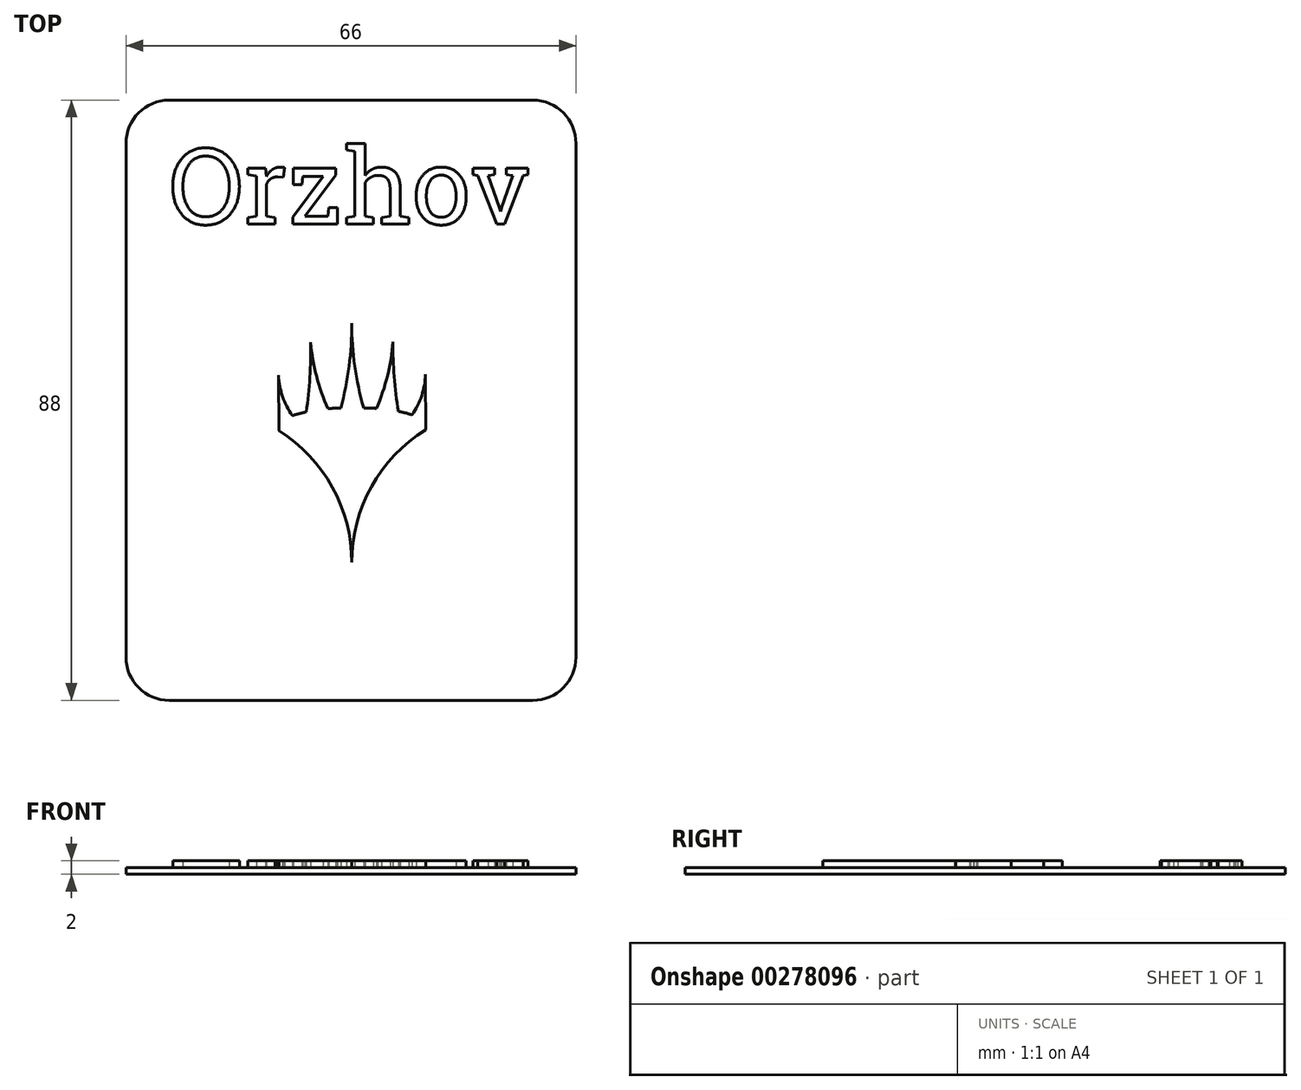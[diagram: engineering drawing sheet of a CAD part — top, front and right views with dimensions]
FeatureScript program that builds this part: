
annotation { "Feature Type Name" : "Feature", "Feature Type Description" : "" }
export const myFeature = defineFeature(function(context is Context, id is Id, definition is map)
    precondition{}
    {
        {
            var Q0;
            Q0=qCreatedBy(makeId("Top.planeOp"),FACE);
            var sketch = newSketch(context, id + "F0", { "sketchPlane" : qUnion([Q0])});
            skLineSegment(sketch, "E0.bottom", {"start": v(-27.42, 35.05) * mm, "end": v(29.8, 35.05) * mm});
            skLineSegment(sketch, "E0.top", {"start": v(-27.42, -41.25) * mm, "end": v(29.8, -41.25) * mm});
            skLineSegment(sketch, "E0.left", {"start": v(-27.42, 35.05) * mm, "end": v(-27.42, -41.25) * mm});
            skLineSegment(sketch, "E0.right", {"start": v(29.8, 35.05) * mm, "end": v(29.8, -41.25) * mm});
            skArc(sketch, "E1", {"start": v(0.12, -23.8) * mm, "mid": v(-2.72, -12.76) * mm, "end": v(-10.54, -4.47) * mm});
            skArc(sketch, "E2", {"start": v(10.94, -4.34) * mm, "mid": v(3, -12.67) * mm, "end": v(0.12, -23.8) * mm});
            skLineSegment(sketch, "E3", {"start": v(-10.54, -4.47) * mm, "end": v(-10.62, 4.28) * mm});
            skArc(sketch, "E4", {"start": v(-5.93, 8.51) * mm, "mid": v(-5.06, 3.53) * mm, "end": v(-3.38, -1.24) * mm});
            skArc(sketch, "E5", {"start": v(-10.62, 4.28) * mm, "mid": v(-10.13, 0.85) * mm, "end": v(-8.59, -2.24) * mm});
            skArc(sketch, "E6", {"start": v(-6.58, -1.72) * mm, "mid": v(-7.6, -1.95) * mm, "end": v(-8.59, -2.24) * mm});
            skArc(sketch, "E7", {"start": v(-1.5, -1.15) * mm, "mid": v(-2.44, -1.17) * mm, "end": v(-3.38, -1.24) * mm});
            skArc(sketch, "E8", {"start": v(-1.5, -1.15) * mm, "mid": v(-0.28, 5.01) * mm, "end": v(0.1, 11.29) * mm});
            skArc(sketch, "E9.MirrorCS", {"start": v(1.86, -1.13) * mm, "mid": v(0.56, 5.02) * mm, "end": v(0.1, 11.29) * mm});
            skArc(sketch, "E10", {"start": v(-6.58, -1.72) * mm, "mid": v(-6.02, 3.38) * mm, "end": v(-5.93, 8.51) * mm});
            skLineSegment(sketch, "E11.MirrorCS", {"start": v(10.94, -4.34) * mm, "end": v(10.9, 4.4) * mm});
            skArc(sketch, "E12.MirrorCS", {"start": v(10.9, 4.4) * mm, "mid": v(10.46, 0.98) * mm, "end": v(8.96, -2.14) * mm});
            skArc(sketch, "E13.MirrorCS", {"start": v(6.94, -1.64) * mm, "mid": v(7.96, -1.85) * mm, "end": v(8.96, -2.14) * mm});
            skArc(sketch, "E14.MirrorCS", {"start": v(6.94, -1.64) * mm, "mid": v(6.33, 3.46) * mm, "end": v(6.16, 8.59) * mm});
            skArc(sketch, "E15.MirrorCS", {"start": v(6.16, 8.59) * mm, "mid": v(5.36, 3.6) * mm, "end": v(3.73, -1.2) * mm});
            skArc(sketch, "E16.MirrorCS", {"start": v(1.86, -1.13) * mm, "mid": v(2.8, -1.13) * mm, "end": v(3.73, -1.2) * mm});
            skSolve(sketch);
        }
        {
            var Q0;
            {var subQ4=sQuery(id+"F0.wireOp",EDGE,"E1");Q0=makeQuery(id+"F0.imprint","IMPRINT",FACE,{"disambiguationData":[TD([[makeQuery(id+"F0.imprint","IMPRINT",EDGE,{"derivedFrom":subQ4}),-1.0]])]});}
            extrude(context, id + "F1", {"entities" : qUnion([Q0]), "depth" : 2 * mm});
        }
        {
            var Q0;
            Q0=qCreatedBy(makeId("Top.planeOp"),FACE);
            var sketch = newSketch(context, id + "F2", { "sketchPlane" : qUnion([Q0])});
            skLineSegment(sketch, "E17.bottom", {"start": v(-26.65, 44) * mm, "end": v(26.65, 44) * mm});
            skLineSegment(sketch, "E17.top", {"start": v(-26.65, -44) * mm, "end": v(26.65, -44) * mm});
            skLineSegment(sketch, "E17.left", {"start": v(-33, 37.65) * mm, "end": v(-33, -37.65) * mm});
            skLineSegment(sketch, "E17.right", {"start": v(33, 37.65) * mm, "end": v(33, -37.65) * mm});
            skPoint(sketch, "E18.visualSharp", {"position": v(-33, 44) * mm});
            skArc(sketch, "E18.filletArc", {"start": v(-26.65, 44) * mm, "mid": v(-31.14, 42.14) * mm, "end": v(-33, 37.65) * mm});
            skPoint(sketch, "E19.visualSharp", {"position": v(33, 44) * mm});
            skArc(sketch, "E19.filletArc", {"start": v(33, 37.65) * mm, "mid": v(31.14, 42.14) * mm, "end": v(26.65, 44) * mm});
            skPoint(sketch, "E20.visualSharp", {"position": v(-33, -44) * mm});
            skArc(sketch, "E20.filletArc", {"start": v(-33, -37.65) * mm, "mid": v(-31.14, -42.14) * mm, "end": v(-26.65, -44) * mm});
            skPoint(sketch, "E21.visualSharp", {"position": v(33, -44) * mm});
            skArc(sketch, "E21.filletArc", {"start": v(26.65, -44) * mm, "mid": v(31.14, -42.14) * mm, "end": v(33, -37.65) * mm});
            skSolve(sketch);
        }
        {
            var Q0;
            Q0=makeQuery(id+"F2.imprint","IMPRINT",FACE,{"disambiguationData":[TD([[makeQuery(id+"F2.imprint","IMPRINT",EDGE,{"derivedFrom":sQuery(id+"F2.wireOp",EDGE,"E17.bottom")}),-1.0]])]});
            extrude(context, id + "F3", {"entities" : qUnion([Q0]), "operationType" : NewBodyOperationType.ADD, "depth" : 1 * mm});
        }
        {
            var Q0;
            Q0=qCreatedBy(makeId("Top.planeOp"),FACE);
            var sketch = newSketch(context, id + "F4", { "sketchPlane" : qUnion([Q0])});
            skText(sketch, "E22", { "text": "Orzhov", "fontName": "RobotoSlab-Regular.ttf"});
            const initialGuessF4  = {"E22": [-0.02674, 0.02583, 1, 0, 0.01118]};
            skSetInitialGuess(sketch, initialGuessF4);
            skSolve(sketch);
        }
        {
            var Q0;
            Q0 = qSketchRegion(id + "F4", true);
            extrude(context, id + "F5", {"entities" : qUnion([Q0]), "operationType" : NewBodyOperationType.ADD, "depth" : 2 * mm});
        }
    });
